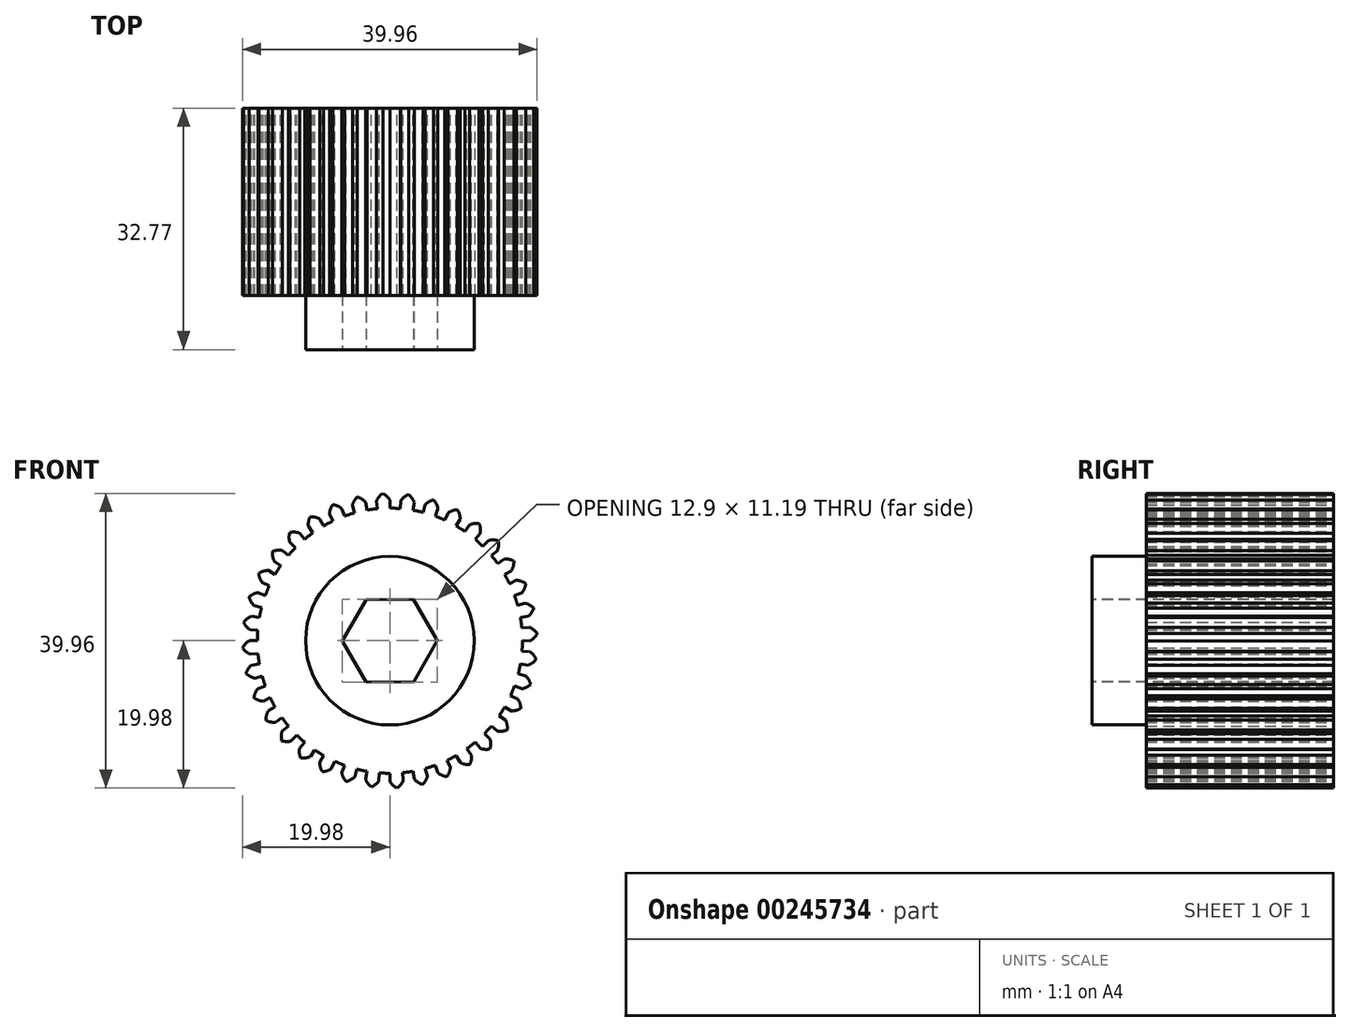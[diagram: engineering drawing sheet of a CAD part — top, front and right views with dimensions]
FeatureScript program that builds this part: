
annotation { "Feature Type Name" : "Feature", "Feature Type Description" : "" }
export const myFeature = defineFeature(function(context is Context, id is Id, definition is map)
    precondition{}
    {
        {
            var Q0;
            Q0=qCreatedBy(makeId("Front.planeOp"),FACE);
            var sketch = newSketch(context, id + "F0", { "sketchPlane" : qUnion([Q0])});
            skArc(sketch, "E0", {"start": v(0, 19.05) * mm, "mid": v(0, 19.05) * mm, "end": v(0, 19.05) * mm});
            skArc(sketch, "E1", {"start": v(-4.8, 17.33) * mm, "mid": v(-5.48, 17.13) * mm, "end": v(-6.15, 16.9) * mm});
            skLineSegment(sketch, "E2", {"start": v(-1.56, 17.83) * mm, "end": v(-1.57, 17.91) * mm});
            skLineSegment(sketch, "E3", {"start": v(0, 16.67) * mm, "end": v(0, 16.67) * mm});
            skLineSegment(sketch, "E4", {"start": v(-0.86, 17.88) * mm, "end": v(-0.86, 17.96) * mm});
            skArc(sketch, "E5.trimOffspring", {"start": v(0, 19.05) * mm, "mid": v(-0.4, 19.58) * mm, "end": v(-0.96, 19.98) * mm});
            skLineSegment(sketch, "E6.trimOffspring", {"start": v(0, 19.05) * mm, "end": v(0, 19.06) * mm});
            skArc(sketch, "E7.trimOffspring", {"start": v(-4.41, 17.44) * mm, "mid": v(-4.41, 17.44) * mm, "end": v(-4.41, 17.43) * mm});
            skPoint(sketch, "E8.trimOffspring.end.orphan", {"position": v(0, 30.11) * mm});
            skPoint(sketch, "E9.trimOffspring.end.orphan", {"position": v(-1.44, 30.11) * mm});
            skPoint(sketch, "E10.trimOffspring.end.orphan", {"position": v(-2.63, 30.11) * mm});
            skPoint(sketch, "E11.orphan", {"position": v(-14.18, 19.05) * mm});
            skPoint(sketch, "E12.trimOffspring.end.orphan", {"position": v(-14.18, 13.89) * mm});
            skLineSegment(sketch, "E13.trimOffspring", {"start": v(-1.66, 18.98) * mm, "end": v(-1.67, 19.05) * mm});
            skArc(sketch, "E14.trimOffspring", {"start": v(0.32, 17.9) * mm, "mid": v(0.32, 17.94) * mm, "end": v(0.32, 17.98) * mm});
            skLineSegment(sketch, "E15.trimOffspring", {"start": v(0, 17.9) * mm, "end": v(0, 17.98) * mm});
            skLineSegment(sketch, "E16", {"start": v(0, 19.05) * mm, "end": v(0, 17.98) * mm});
            skArc(sketch, "E17.MirrorCS", {"start": v(-1.83, 18.96) * mm, "mid": v(-1.46, 19.53) * mm, "end": v(-0.96, 19.98) * mm});
            skLineSegment(sketch, "E18.MirrorCS", {"start": v(-1.83, 18.96) * mm, "end": v(-1.72, 17.9) * mm});
            skArc(sketch, "E19.1.0", {"start": v(-3.3, 18.76) * mm, "mid": v(-3.8, 19.21) * mm, "end": v(-4.41, 19.5) * mm});
            skLineSegment(sketch, "E19.1.1", {"start": v(-3.3, 18.76) * mm, "end": v(-3.12, 17.7) * mm});
            skArc(sketch, "E19.1.2", {"start": v(-5.1, 18.36) * mm, "mid": v(-4.83, 18.98) * mm, "end": v(-4.41, 19.5) * mm});
            skLineSegment(sketch, "E19.1.3", {"start": v(-5.1, 18.36) * mm, "end": v(-4.8, 17.33) * mm});
            skArc(sketch, "E19.2.0", {"start": v(-6.51, 17.9) * mm, "mid": v(-7.08, 18.26) * mm, "end": v(-7.73, 18.44) * mm});
            skLineSegment(sketch, "E19.2.1", {"start": v(-6.51, 17.9) * mm, "end": v(-6.15, 16.9) * mm});
            skArc(sketch, "E19.2.2", {"start": v(-8.2, 17.2) * mm, "mid": v(-8.06, 17.85) * mm, "end": v(-7.73, 18.44) * mm});
            skLineSegment(sketch, "E19.2.3", {"start": v(-8.2, 17.2) * mm, "end": v(-7.74, 16.23) * mm});
            skArc(sketch, "E19.3.0", {"start": v(-9.52, 16.5) * mm, "mid": v(-10.15, 16.75) * mm, "end": v(-10.82, 16.82) * mm});
            skLineSegment(sketch, "E19.3.1", {"start": v(-9.52, 16.5) * mm, "end": v(-9, 15.57) * mm});
            skArc(sketch, "E19.3.2", {"start": v(-11.06, 15.5) * mm, "mid": v(-11.03, 16.18) * mm, "end": v(-10.82, 16.82) * mm});
            skLineSegment(sketch, "E19.3.3", {"start": v(-11.06, 15.5) * mm, "end": v(-10.44, 14.64) * mm});
            skArc(sketch, "E19.4.0", {"start": v(-12.24, 14.6) * mm, "mid": v(-12.9, 14.74) * mm, "end": v(-13.57, 14.69) * mm});
            skLineSegment(sketch, "E19.4.1", {"start": v(-12.24, 14.6) * mm, "end": v(-11.56, 13.78) * mm});
            skArc(sketch, "E19.4.2", {"start": v(-13.59, 13.35) * mm, "mid": v(-13.68, 14.02) * mm, "end": v(-13.57, 14.69) * mm});
            skLineSegment(sketch, "E19.4.3", {"start": v(-13.59, 13.35) * mm, "end": v(-12.82, 12.6) * mm});
            skArc(sketch, "E19.5.0", {"start": v(-14.59, 12.25) * mm, "mid": v(-15.26, 12.27) * mm, "end": v(-15.92, 12.1) * mm});
            skLineSegment(sketch, "E19.5.1", {"start": v(-14.59, 12.25) * mm, "end": v(-13.78, 11.56) * mm});
            skArc(sketch, "E19.5.2", {"start": v(-15.7, 10.8) * mm, "mid": v(-15.9, 11.43) * mm, "end": v(-15.92, 12.1) * mm});
            skLineSegment(sketch, "E19.5.3", {"start": v(-15.7, 10.8) * mm, "end": v(-14.82, 10.2) * mm});
            skArc(sketch, "E19.6.0", {"start": v(-16.5, 9.53) * mm, "mid": v(-17.16, 9.44) * mm, "end": v(-17.78, 9.16) * mm});
            skLineSegment(sketch, "E19.6.1", {"start": v(-16.5, 9.53) * mm, "end": v(-15.57, 9) * mm});
            skArc(sketch, "E19.6.2", {"start": v(-17.33, 7.9) * mm, "mid": v(-17.65, 8.5) * mm, "end": v(-17.78, 9.16) * mm});
            skLineSegment(sketch, "E19.6.3", {"start": v(-17.33, 7.9) * mm, "end": v(-16.36, 7.46) * mm});
            skArc(sketch, "E19.7.0", {"start": v(-17.9, 6.52) * mm, "mid": v(-18.54, 6.31) * mm, "end": v(-19.1, 5.93) * mm});
            skLineSegment(sketch, "E19.7.1", {"start": v(-17.9, 6.52) * mm, "end": v(-16.9, 6.15) * mm});
            skArc(sketch, "E19.7.2", {"start": v(-18.44, 4.77) * mm, "mid": v(-18.85, 5.3) * mm, "end": v(-19.1, 5.93) * mm});
            skLineSegment(sketch, "E19.7.3", {"start": v(-18.44, 4.77) * mm, "end": v(-17.4, 4.5) * mm});
            skArc(sketch, "E19.8.0", {"start": v(-18.76, 3.31) * mm, "mid": v(-19.36, 3) * mm, "end": v(-19.84, 2.53) * mm});
            skLineSegment(sketch, "E19.8.1", {"start": v(-18.76, 3.31) * mm, "end": v(-17.7, 3.12) * mm});
            skArc(sketch, "E19.8.2", {"start": v(-19, 1.5) * mm, "mid": v(-19.49, 1.95) * mm, "end": v(-19.84, 2.53) * mm});
            skLineSegment(sketch, "E19.8.3", {"start": v(-19, 1.5) * mm, "end": v(-17.93, 1.42) * mm});
            skArc(sketch, "E19.9.0", {"start": v(-19.05, 0) * mm, "mid": v(-19.58, -0.4) * mm, "end": v(-19.98, -0.96) * mm});
            skLineSegment(sketch, "E19.9.1", {"start": v(-19.05, 0) * mm, "end": v(-17.98, 0) * mm});
            skArc(sketch, "E19.9.2", {"start": v(-18.96, -1.83) * mm, "mid": v(-19.53, -1.46) * mm, "end": v(-19.98, -0.96) * mm});
            skLineSegment(sketch, "E19.9.3", {"start": v(-18.96, -1.83) * mm, "end": v(-17.9, -1.72) * mm});
            skArc(sketch, "E19.10.0", {"start": v(-18.76, -3.3) * mm, "mid": v(-19.21, -3.8) * mm, "end": v(-19.5, -4.41) * mm});
            skLineSegment(sketch, "E19.10.1", {"start": v(-18.76, -3.3) * mm, "end": v(-17.7, -3.12) * mm});
            skArc(sketch, "E19.10.2", {"start": v(-18.36, -5.1) * mm, "mid": v(-18.98, -4.83) * mm, "end": v(-19.5, -4.41) * mm});
            skLineSegment(sketch, "E19.10.3", {"start": v(-18.36, -5.1) * mm, "end": v(-17.33, -4.8) * mm});
            skArc(sketch, "E19.11.0", {"start": v(-17.9, -6.51) * mm, "mid": v(-18.26, -7.08) * mm, "end": v(-18.44, -7.73) * mm});
            skLineSegment(sketch, "E19.11.1", {"start": v(-17.9, -6.51) * mm, "end": v(-16.9, -6.15) * mm});
            skArc(sketch, "E19.11.2", {"start": v(-17.2, -8.2) * mm, "mid": v(-17.85, -8.06) * mm, "end": v(-18.44, -7.73) * mm});
            skLineSegment(sketch, "E19.11.3", {"start": v(-17.2, -8.2) * mm, "end": v(-16.23, -7.74) * mm});
            skArc(sketch, "E19.12.0", {"start": v(-16.5, -9.52) * mm, "mid": v(-16.75, -10.15) * mm, "end": v(-16.82, -10.82) * mm});
            skLineSegment(sketch, "E19.12.1", {"start": v(-16.5, -9.52) * mm, "end": v(-15.57, -9) * mm});
            skArc(sketch, "E19.12.2", {"start": v(-15.5, -11.06) * mm, "mid": v(-16.18, -11.03) * mm, "end": v(-16.82, -10.82) * mm});
            skLineSegment(sketch, "E19.12.3", {"start": v(-15.5, -11.06) * mm, "end": v(-14.64, -10.44) * mm});
            skArc(sketch, "E19.13.0", {"start": v(-14.6, -12.24) * mm, "mid": v(-14.74, -12.9) * mm, "end": v(-14.69, -13.57) * mm});
            skLineSegment(sketch, "E19.13.1", {"start": v(-14.6, -12.24) * mm, "end": v(-13.78, -11.56) * mm});
            skArc(sketch, "E19.13.2", {"start": v(-13.35, -13.59) * mm, "mid": v(-14.02, -13.68) * mm, "end": v(-14.69, -13.57) * mm});
            skLineSegment(sketch, "E19.13.3", {"start": v(-13.35, -13.59) * mm, "end": v(-12.6, -12.82) * mm});
            skArc(sketch, "E19.14.0", {"start": v(-12.25, -14.59) * mm, "mid": v(-12.27, -15.26) * mm, "end": v(-12.1, -15.92) * mm});
            skLineSegment(sketch, "E19.14.1", {"start": v(-12.25, -14.59) * mm, "end": v(-11.56, -13.78) * mm});
            skArc(sketch, "E19.14.2", {"start": v(-10.8, -15.7) * mm, "mid": v(-11.43, -15.9) * mm, "end": v(-12.1, -15.92) * mm});
            skLineSegment(sketch, "E19.14.3", {"start": v(-10.8, -15.7) * mm, "end": v(-10.2, -14.82) * mm});
            skArc(sketch, "E19.15.0", {"start": v(-9.53, -16.5) * mm, "mid": v(-9.44, -17.16) * mm, "end": v(-9.16, -17.78) * mm});
            skLineSegment(sketch, "E19.15.1", {"start": v(-9.53, -16.5) * mm, "end": v(-9, -15.57) * mm});
            skArc(sketch, "E19.15.2", {"start": v(-7.9, -17.33) * mm, "mid": v(-8.5, -17.65) * mm, "end": v(-9.16, -17.78) * mm});
            skLineSegment(sketch, "E19.15.3", {"start": v(-7.9, -17.33) * mm, "end": v(-7.46, -16.36) * mm});
            skArc(sketch, "E19.16.0", {"start": v(-6.52, -17.9) * mm, "mid": v(-6.31, -18.54) * mm, "end": v(-5.93, -19.1) * mm});
            skLineSegment(sketch, "E19.16.1", {"start": v(-6.52, -17.9) * mm, "end": v(-6.15, -16.9) * mm});
            skArc(sketch, "E19.16.2", {"start": v(-4.77, -18.44) * mm, "mid": v(-5.3, -18.85) * mm, "end": v(-5.93, -19.1) * mm});
            skLineSegment(sketch, "E19.16.3", {"start": v(-4.77, -18.44) * mm, "end": v(-4.5, -17.4) * mm});
            skArc(sketch, "E19.17.0", {"start": v(-3.31, -18.76) * mm, "mid": v(-3, -19.36) * mm, "end": v(-2.53, -19.84) * mm});
            skLineSegment(sketch, "E19.17.1", {"start": v(-3.31, -18.76) * mm, "end": v(-3.12, -17.7) * mm});
            skArc(sketch, "E19.17.2", {"start": v(-1.5, -19) * mm, "mid": v(-1.95, -19.49) * mm, "end": v(-2.53, -19.84) * mm});
            skLineSegment(sketch, "E19.17.3", {"start": v(-1.5, -19) * mm, "end": v(-1.42, -17.93) * mm});
            skArc(sketch, "E19.18.0", {"start": v(0, -19.05) * mm, "mid": v(0.4, -19.58) * mm, "end": v(0.96, -19.98) * mm});
            skLineSegment(sketch, "E19.18.1", {"start": v(0, -19.05) * mm, "end": v(0, -17.98) * mm});
            skArc(sketch, "E19.18.2", {"start": v(1.83, -18.96) * mm, "mid": v(1.46, -19.53) * mm, "end": v(0.96, -19.98) * mm});
            skLineSegment(sketch, "E19.18.3", {"start": v(1.83, -18.96) * mm, "end": v(1.72, -17.9) * mm});
            skArc(sketch, "E19.19.0", {"start": v(3.3, -18.76) * mm, "mid": v(3.8, -19.21) * mm, "end": v(4.41, -19.5) * mm});
            skLineSegment(sketch, "E19.19.1", {"start": v(3.3, -18.76) * mm, "end": v(3.12, -17.7) * mm});
            skArc(sketch, "E19.19.2", {"start": v(5.1, -18.36) * mm, "mid": v(4.83, -18.98) * mm, "end": v(4.41, -19.5) * mm});
            skLineSegment(sketch, "E19.19.3", {"start": v(5.1, -18.36) * mm, "end": v(4.8, -17.33) * mm});
            skArc(sketch, "E19.20.0", {"start": v(6.51, -17.9) * mm, "mid": v(7.08, -18.26) * mm, "end": v(7.73, -18.44) * mm});
            skLineSegment(sketch, "E19.20.1", {"start": v(6.51, -17.9) * mm, "end": v(6.15, -16.9) * mm});
            skArc(sketch, "E19.20.2", {"start": v(8.2, -17.2) * mm, "mid": v(8.06, -17.85) * mm, "end": v(7.73, -18.44) * mm});
            skLineSegment(sketch, "E19.20.3", {"start": v(8.2, -17.2) * mm, "end": v(7.74, -16.23) * mm});
            skArc(sketch, "E19.21.0", {"start": v(9.52, -16.5) * mm, "mid": v(10.15, -16.75) * mm, "end": v(10.82, -16.82) * mm});
            skLineSegment(sketch, "E19.21.1", {"start": v(9.52, -16.5) * mm, "end": v(9, -15.57) * mm});
            skArc(sketch, "E19.21.2", {"start": v(11.06, -15.5) * mm, "mid": v(11.03, -16.18) * mm, "end": v(10.82, -16.82) * mm});
            skLineSegment(sketch, "E19.21.3", {"start": v(11.06, -15.5) * mm, "end": v(10.44, -14.64) * mm});
            skArc(sketch, "E19.22.0", {"start": v(12.24, -14.6) * mm, "mid": v(12.9, -14.74) * mm, "end": v(13.57, -14.69) * mm});
            skLineSegment(sketch, "E19.22.1", {"start": v(12.24, -14.6) * mm, "end": v(11.56, -13.78) * mm});
            skArc(sketch, "E19.22.2", {"start": v(13.59, -13.35) * mm, "mid": v(13.68, -14.02) * mm, "end": v(13.57, -14.69) * mm});
            skLineSegment(sketch, "E19.22.3", {"start": v(13.59, -13.35) * mm, "end": v(12.82, -12.6) * mm});
            skArc(sketch, "E19.23.0", {"start": v(14.59, -12.25) * mm, "mid": v(15.26, -12.27) * mm, "end": v(15.92, -12.1) * mm});
            skLineSegment(sketch, "E19.23.1", {"start": v(14.59, -12.25) * mm, "end": v(13.78, -11.56) * mm});
            skArc(sketch, "E19.23.2", {"start": v(15.7, -10.8) * mm, "mid": v(15.9, -11.43) * mm, "end": v(15.92, -12.1) * mm});
            skLineSegment(sketch, "E19.23.3", {"start": v(15.7, -10.8) * mm, "end": v(14.82, -10.2) * mm});
            skArc(sketch, "E19.24.0", {"start": v(16.5, -9.53) * mm, "mid": v(17.16, -9.44) * mm, "end": v(17.78, -9.16) * mm});
            skLineSegment(sketch, "E19.24.1", {"start": v(16.5, -9.53) * mm, "end": v(15.57, -9) * mm});
            skArc(sketch, "E19.24.2", {"start": v(17.33, -7.9) * mm, "mid": v(17.65, -8.5) * mm, "end": v(17.78, -9.16) * mm});
            skLineSegment(sketch, "E19.24.3", {"start": v(17.33, -7.9) * mm, "end": v(16.36, -7.46) * mm});
            skArc(sketch, "E19.25.0", {"start": v(17.9, -6.52) * mm, "mid": v(18.54, -6.31) * mm, "end": v(19.1, -5.93) * mm});
            skLineSegment(sketch, "E19.25.1", {"start": v(17.9, -6.52) * mm, "end": v(16.9, -6.15) * mm});
            skArc(sketch, "E19.25.2", {"start": v(18.44, -4.77) * mm, "mid": v(18.85, -5.3) * mm, "end": v(19.1, -5.93) * mm});
            skLineSegment(sketch, "E19.25.3", {"start": v(18.44, -4.77) * mm, "end": v(17.4, -4.5) * mm});
            skArc(sketch, "E19.26.0", {"start": v(18.76, -3.31) * mm, "mid": v(19.36, -3) * mm, "end": v(19.84, -2.53) * mm});
            skLineSegment(sketch, "E19.26.1", {"start": v(18.76, -3.31) * mm, "end": v(17.7, -3.12) * mm});
            skArc(sketch, "E19.26.2", {"start": v(19, -1.5) * mm, "mid": v(19.49, -1.95) * mm, "end": v(19.84, -2.53) * mm});
            skLineSegment(sketch, "E19.26.3", {"start": v(19, -1.5) * mm, "end": v(17.93, -1.42) * mm});
            skArc(sketch, "E19.27.0", {"start": v(19.05, 0) * mm, "mid": v(19.58, 0.4) * mm, "end": v(19.98, 0.96) * mm});
            skLineSegment(sketch, "E19.27.1", {"start": v(19.05, 0) * mm, "end": v(17.98, 0) * mm});
            skArc(sketch, "E19.27.2", {"start": v(18.96, 1.83) * mm, "mid": v(19.53, 1.46) * mm, "end": v(19.98, 0.96) * mm});
            skLineSegment(sketch, "E19.27.3", {"start": v(18.96, 1.83) * mm, "end": v(17.9, 1.72) * mm});
            skArc(sketch, "E19.28.0", {"start": v(18.76, 3.3) * mm, "mid": v(19.21, 3.8) * mm, "end": v(19.5, 4.41) * mm});
            skLineSegment(sketch, "E19.28.1", {"start": v(18.76, 3.3) * mm, "end": v(17.7, 3.12) * mm});
            skArc(sketch, "E19.28.2", {"start": v(18.36, 5.1) * mm, "mid": v(18.98, 4.83) * mm, "end": v(19.5, 4.41) * mm});
            skLineSegment(sketch, "E19.28.3", {"start": v(18.36, 5.1) * mm, "end": v(17.33, 4.8) * mm});
            skArc(sketch, "E19.29.0", {"start": v(17.9, 6.51) * mm, "mid": v(18.26, 7.08) * mm, "end": v(18.44, 7.73) * mm});
            skLineSegment(sketch, "E19.29.1", {"start": v(17.9, 6.51) * mm, "end": v(16.9, 6.15) * mm});
            skArc(sketch, "E19.29.2", {"start": v(17.2, 8.2) * mm, "mid": v(17.85, 8.06) * mm, "end": v(18.44, 7.73) * mm});
            skLineSegment(sketch, "E19.29.3", {"start": v(17.2, 8.2) * mm, "end": v(16.23, 7.74) * mm});
            skArc(sketch, "E19.30.0", {"start": v(16.5, 9.52) * mm, "mid": v(16.75, 10.15) * mm, "end": v(16.82, 10.82) * mm});
            skLineSegment(sketch, "E19.30.1", {"start": v(16.5, 9.52) * mm, "end": v(15.57, 9) * mm});
            skArc(sketch, "E19.30.2", {"start": v(15.5, 11.06) * mm, "mid": v(16.18, 11.03) * mm, "end": v(16.82, 10.82) * mm});
            skLineSegment(sketch, "E19.30.3", {"start": v(15.5, 11.06) * mm, "end": v(14.64, 10.44) * mm});
            skArc(sketch, "E19.31.0", {"start": v(14.6, 12.24) * mm, "mid": v(14.74, 12.9) * mm, "end": v(14.69, 13.57) * mm});
            skLineSegment(sketch, "E19.31.1", {"start": v(14.6, 12.24) * mm, "end": v(13.78, 11.56) * mm});
            skArc(sketch, "E19.31.2", {"start": v(13.35, 13.59) * mm, "mid": v(14.02, 13.68) * mm, "end": v(14.69, 13.57) * mm});
            skLineSegment(sketch, "E19.31.3", {"start": v(13.35, 13.59) * mm, "end": v(12.6, 12.82) * mm});
            skArc(sketch, "E19.32.0", {"start": v(12.25, 14.59) * mm, "mid": v(12.27, 15.26) * mm, "end": v(12.1, 15.92) * mm});
            skLineSegment(sketch, "E19.32.1", {"start": v(12.25, 14.59) * mm, "end": v(11.56, 13.78) * mm});
            skArc(sketch, "E19.32.2", {"start": v(10.8, 15.7) * mm, "mid": v(11.43, 15.9) * mm, "end": v(12.1, 15.92) * mm});
            skLineSegment(sketch, "E19.32.3", {"start": v(10.8, 15.7) * mm, "end": v(10.2, 14.82) * mm});
            skArc(sketch, "E19.33.0", {"start": v(9.53, 16.5) * mm, "mid": v(9.44, 17.16) * mm, "end": v(9.16, 17.78) * mm});
            skLineSegment(sketch, "E19.33.1", {"start": v(9.53, 16.5) * mm, "end": v(9, 15.57) * mm});
            skArc(sketch, "E19.33.2", {"start": v(7.9, 17.33) * mm, "mid": v(8.5, 17.65) * mm, "end": v(9.16, 17.78) * mm});
            skLineSegment(sketch, "E19.33.3", {"start": v(7.9, 17.33) * mm, "end": v(7.46, 16.36) * mm});
            skArc(sketch, "E19.34.0", {"start": v(6.52, 17.9) * mm, "mid": v(6.31, 18.54) * mm, "end": v(5.93, 19.1) * mm});
            skLineSegment(sketch, "E19.34.1", {"start": v(6.52, 17.9) * mm, "end": v(6.15, 16.9) * mm});
            skArc(sketch, "E19.34.2", {"start": v(4.77, 18.44) * mm, "mid": v(5.3, 18.85) * mm, "end": v(5.93, 19.1) * mm});
            skLineSegment(sketch, "E19.34.3", {"start": v(4.77, 18.44) * mm, "end": v(4.5, 17.4) * mm});
            skArc(sketch, "E19.35.0", {"start": v(3.31, 18.76) * mm, "mid": v(3, 19.36) * mm, "end": v(2.53, 19.84) * mm});
            skLineSegment(sketch, "E19.35.1", {"start": v(3.31, 18.76) * mm, "end": v(3.12, 17.7) * mm});
            skArc(sketch, "E19.35.2", {"start": v(1.5, 19) * mm, "mid": v(1.95, 19.49) * mm, "end": v(2.53, 19.84) * mm});
            skLineSegment(sketch, "E19.35.3", {"start": v(1.5, 19) * mm, "end": v(1.42, 17.93) * mm});
            skArc(sketch, "E20.trimOffspring", {"start": v(-7.74, 16.23) * mm, "mid": v(-8.37, 15.92) * mm, "end": v(-9, 15.57) * mm});
            skArc(sketch, "E21.trimOffspring", {"start": v(-10.44, 14.64) * mm, "mid": v(-11, 14.22) * mm, "end": v(-11.56, 13.78) * mm});
            skArc(sketch, "E22.trimOffspring", {"start": v(-12.82, 12.6) * mm, "mid": v(-13.3, 12.1) * mm, "end": v(-13.78, 11.56) * mm});
            skArc(sketch, "E23.trimOffspring", {"start": v(-14.82, 10.2) * mm, "mid": v(-15.2, 9.6) * mm, "end": v(-15.57, 9) * mm});
            skArc(sketch, "E24.trimOffspring", {"start": v(-16.36, 7.46) * mm, "mid": v(-16.64, 6.81) * mm, "end": v(-16.9, 6.15) * mm});
            skArc(sketch, "E25.trimOffspring", {"start": v(-17.4, 4.5) * mm, "mid": v(-17.57, 3.82) * mm, "end": v(-17.7, 3.12) * mm});
            skArc(sketch, "E26.trimOffspring", {"start": v(-17.93, 1.42) * mm, "mid": v(-17.97, 0.7) * mm, "end": v(-17.98, 0) * mm});
            skArc(sketch, "E27.trimOffspring", {"start": v(-17.9, -1.72) * mm, "mid": v(-17.82, -2.42) * mm, "end": v(-17.7, -3.12) * mm});
            skArc(sketch, "E28.trimOffspring", {"start": v(-17.33, -4.8) * mm, "mid": v(-17.13, -5.48) * mm, "end": v(-16.9, -6.15) * mm});
            skArc(sketch, "E29.trimOffspring", {"start": v(-16.23, -7.74) * mm, "mid": v(-15.92, -8.37) * mm, "end": v(-15.57, -9) * mm});
            skArc(sketch, "E30.trimOffspring", {"start": v(-14.64, -10.44) * mm, "mid": v(-14.22, -11) * mm, "end": v(-13.78, -11.56) * mm});
            skArc(sketch, "E31.trimOffspring", {"start": v(-12.6, -12.82) * mm, "mid": v(-12.1, -13.3) * mm, "end": v(-11.56, -13.78) * mm});
            skArc(sketch, "E32.trimOffspring", {"start": v(-10.2, -14.82) * mm, "mid": v(-9.6, -15.2) * mm, "end": v(-9, -15.57) * mm});
            skArc(sketch, "E33.trimOffspring", {"start": v(-7.46, -16.36) * mm, "mid": v(-6.81, -16.64) * mm, "end": v(-6.15, -16.9) * mm});
            skArc(sketch, "E34.trimOffspring", {"start": v(-4.5, -17.4) * mm, "mid": v(-3.82, -17.57) * mm, "end": v(-3.12, -17.7) * mm});
            skArc(sketch, "E35.trimOffspring", {"start": v(-1.42, -17.93) * mm, "mid": v(-0.7, -17.97) * mm, "end": v(0, -17.98) * mm});
            skArc(sketch, "E36.trimOffspring", {"start": v(1.72, -17.9) * mm, "mid": v(2.42, -17.82) * mm, "end": v(3.12, -17.7) * mm});
            skArc(sketch, "E37.trimOffspring", {"start": v(4.8, -17.33) * mm, "mid": v(5.48, -17.13) * mm, "end": v(6.15, -16.9) * mm});
            skArc(sketch, "E38.trimOffspring", {"start": v(7.74, -16.23) * mm, "mid": v(8.37, -15.92) * mm, "end": v(9, -15.57) * mm});
            skArc(sketch, "E39.trimOffspring", {"start": v(10.44, -14.64) * mm, "mid": v(11, -14.22) * mm, "end": v(11.56, -13.78) * mm});
            skArc(sketch, "E40.trimOffspring", {"start": v(12.82, -12.6) * mm, "mid": v(13.3, -12.1) * mm, "end": v(13.78, -11.56) * mm});
            skArc(sketch, "E41.trimOffspring", {"start": v(14.82, -10.2) * mm, "mid": v(15.2, -9.6) * mm, "end": v(15.57, -9) * mm});
            skArc(sketch, "E42.trimOffspring", {"start": v(16.36, -7.46) * mm, "mid": v(16.64, -6.81) * mm, "end": v(16.9, -6.15) * mm});
            skArc(sketch, "E43.trimOffspring", {"start": v(17.4, -4.5) * mm, "mid": v(17.57, -3.82) * mm, "end": v(17.7, -3.12) * mm});
            skArc(sketch, "E44.trimOffspring", {"start": v(17.93, -1.42) * mm, "mid": v(17.97, -0.7) * mm, "end": v(17.98, 0) * mm});
            skArc(sketch, "E45.trimOffspring", {"start": v(17.9, 1.72) * mm, "mid": v(17.82, 2.42) * mm, "end": v(17.7, 3.12) * mm});
            skArc(sketch, "E46.trimOffspring", {"start": v(17.33, 4.8) * mm, "mid": v(17.13, 5.48) * mm, "end": v(16.9, 6.15) * mm});
            skArc(sketch, "E47.trimOffspring", {"start": v(16.23, 7.74) * mm, "mid": v(15.92, 8.37) * mm, "end": v(15.57, 9) * mm});
            skArc(sketch, "E48.trimOffspring", {"start": v(14.64, 10.44) * mm, "mid": v(14.22, 11) * mm, "end": v(13.78, 11.56) * mm});
            skArc(sketch, "E49.trimOffspring", {"start": v(12.6, 12.82) * mm, "mid": v(12.1, 13.3) * mm, "end": v(11.56, 13.78) * mm});
            skArc(sketch, "E50.trimOffspring", {"start": v(10.2, 14.82) * mm, "mid": v(9.6, 15.2) * mm, "end": v(9, 15.57) * mm});
            skArc(sketch, "E51.trimOffspring", {"start": v(7.46, 16.36) * mm, "mid": v(6.81, 16.64) * mm, "end": v(6.15, 16.9) * mm});
            skArc(sketch, "E52.trimOffspring", {"start": v(4.5, 17.4) * mm, "mid": v(3.82, 17.57) * mm, "end": v(3.12, 17.7) * mm});
            skArc(sketch, "E53.trimOffspring", {"start": v(1.42, 17.93) * mm, "mid": v(0.7, 17.97) * mm, "end": v(0, 17.98) * mm});
            skArc(sketch, "E54.trimOffspring", {"start": v(-1.57, 17.91) * mm, "mid": v(-2.35, 17.83) * mm, "end": v(-3.12, 17.7) * mm});
            skSolve(sketch);
        }
        {
            var Q0;
            Q0 = qSketchRegion(id + "F0", true);
            extrude(context, id + "F1", {"entities" : qUnion([Q0]), "depth" : 25.4 * mm});
        }
        {
            var Q0;
            Q0=makeQuery(id+"F1.opExtrude","CAP_FACE",FACE,{"disambiguationData":[OSD([sQuery(id+"F0.wireOp",EDGE,"E1"),sQuery(id+"F0.wireOp",EDGE,"E5.trimOffspring"),sQuery(id+"F0.wireOp",EDGE,"E16"),sQuery(id+"F0.wireOp",EDGE,"E17.MirrorCS"),sQuery(id+"F0.wireOp",EDGE,"E18.MirrorCS"),sQuery(id+"F0.wireOp",EDGE,"E19.1.0"),sQuery(id+"F0.wireOp",EDGE,"E19.1.1"),sQuery(id+"F0.wireOp",EDGE,"E19.1.2"),sQuery(id+"F0.wireOp",EDGE,"E19.1.3"),sQuery(id+"F0.wireOp",EDGE,"E19.2.0"),sQuery(id+"F0.wireOp",EDGE,"E19.2.1"),sQuery(id+"F0.wireOp",EDGE,"E19.2.2"),sQuery(id+"F0.wireOp",EDGE,"E19.2.3"),sQuery(id+"F0.wireOp",EDGE,"E19.3.0"),sQuery(id+"F0.wireOp",EDGE,"E19.3.1"),sQuery(id+"F0.wireOp",EDGE,"E19.3.2"),sQuery(id+"F0.wireOp",EDGE,"E19.3.3"),sQuery(id+"F0.wireOp",EDGE,"E19.4.0"),sQuery(id+"F0.wireOp",EDGE,"E19.4.1"),sQuery(id+"F0.wireOp",EDGE,"E19.4.2"),sQuery(id+"F0.wireOp",EDGE,"E19.4.3"),sQuery(id+"F0.wireOp",EDGE,"E19.5.0"),sQuery(id+"F0.wireOp",EDGE,"E19.5.1"),sQuery(id+"F0.wireOp",EDGE,"E19.5.2"),sQuery(id+"F0.wireOp",EDGE,"E19.5.3"),sQuery(id+"F0.wireOp",EDGE,"E19.6.0"),sQuery(id+"F0.wireOp",EDGE,"E19.6.1"),sQuery(id+"F0.wireOp",EDGE,"E19.6.2"),sQuery(id+"F0.wireOp",EDGE,"E19.6.3"),sQuery(id+"F0.wireOp",EDGE,"E19.7.0"),sQuery(id+"F0.wireOp",EDGE,"E19.7.1"),sQuery(id+"F0.wireOp",EDGE,"E19.7.2"),sQuery(id+"F0.wireOp",EDGE,"E19.7.3"),sQuery(id+"F0.wireOp",EDGE,"E19.8.0"),sQuery(id+"F0.wireOp",EDGE,"E19.8.1"),sQuery(id+"F0.wireOp",EDGE,"E19.8.2"),sQuery(id+"F0.wireOp",EDGE,"E19.8.3"),sQuery(id+"F0.wireOp",EDGE,"E19.9.0"),sQuery(id+"F0.wireOp",EDGE,"E19.9.1"),sQuery(id+"F0.wireOp",EDGE,"E19.9.2"),sQuery(id+"F0.wireOp",EDGE,"E19.9.3"),sQuery(id+"F0.wireOp",EDGE,"E19.10.0"),sQuery(id+"F0.wireOp",EDGE,"E19.10.1"),sQuery(id+"F0.wireOp",EDGE,"E19.10.2"),sQuery(id+"F0.wireOp",EDGE,"E19.10.3"),sQuery(id+"F0.wireOp",EDGE,"E19.11.0"),sQuery(id+"F0.wireOp",EDGE,"E19.11.1"),sQuery(id+"F0.wireOp",EDGE,"E19.11.2"),sQuery(id+"F0.wireOp",EDGE,"E19.11.3"),sQuery(id+"F0.wireOp",EDGE,"E19.12.0"),sQuery(id+"F0.wireOp",EDGE,"E19.12.1"),sQuery(id+"F0.wireOp",EDGE,"E19.12.2"),sQuery(id+"F0.wireOp",EDGE,"E19.12.3"),sQuery(id+"F0.wireOp",EDGE,"E19.13.0"),sQuery(id+"F0.wireOp",EDGE,"E19.13.1"),sQuery(id+"F0.wireOp",EDGE,"E19.13.2"),sQuery(id+"F0.wireOp",EDGE,"E19.13.3"),sQuery(id+"F0.wireOp",EDGE,"E19.14.0"),sQuery(id+"F0.wireOp",EDGE,"E19.14.1"),sQuery(id+"F0.wireOp",EDGE,"E19.14.2"),sQuery(id+"F0.wireOp",EDGE,"E19.14.3"),sQuery(id+"F0.wireOp",EDGE,"E19.15.0"),sQuery(id+"F0.wireOp",EDGE,"E19.15.1"),sQuery(id+"F0.wireOp",EDGE,"E19.15.2"),sQuery(id+"F0.wireOp",EDGE,"E19.15.3"),sQuery(id+"F0.wireOp",EDGE,"E19.16.0"),sQuery(id+"F0.wireOp",EDGE,"E19.16.1"),sQuery(id+"F0.wireOp",EDGE,"E19.16.2"),sQuery(id+"F0.wireOp",EDGE,"E19.16.3"),sQuery(id+"F0.wireOp",EDGE,"E19.17.0"),sQuery(id+"F0.wireOp",EDGE,"E19.17.1"),sQuery(id+"F0.wireOp",EDGE,"E19.17.2"),sQuery(id+"F0.wireOp",EDGE,"E19.17.3"),sQuery(id+"F0.wireOp",EDGE,"E19.18.0"),sQuery(id+"F0.wireOp",EDGE,"E19.18.1"),sQuery(id+"F0.wireOp",EDGE,"E19.18.2"),sQuery(id+"F0.wireOp",EDGE,"E19.18.3"),sQuery(id+"F0.wireOp",EDGE,"E19.19.0"),sQuery(id+"F0.wireOp",EDGE,"E19.19.1"),sQuery(id+"F0.wireOp",EDGE,"E19.19.2"),sQuery(id+"F0.wireOp",EDGE,"E19.19.3"),sQuery(id+"F0.wireOp",EDGE,"E19.20.0"),sQuery(id+"F0.wireOp",EDGE,"E19.20.1"),sQuery(id+"F0.wireOp",EDGE,"E19.20.2"),sQuery(id+"F0.wireOp",EDGE,"E19.20.3"),sQuery(id+"F0.wireOp",EDGE,"E19.21.0"),sQuery(id+"F0.wireOp",EDGE,"E19.21.1"),sQuery(id+"F0.wireOp",EDGE,"E19.21.2"),sQuery(id+"F0.wireOp",EDGE,"E19.21.3"),sQuery(id+"F0.wireOp",EDGE,"E19.22.0"),sQuery(id+"F0.wireOp",EDGE,"E19.22.1"),sQuery(id+"F0.wireOp",EDGE,"E19.22.2"),sQuery(id+"F0.wireOp",EDGE,"E19.22.3"),sQuery(id+"F0.wireOp",EDGE,"E19.23.0"),sQuery(id+"F0.wireOp",EDGE,"E19.23.1"),sQuery(id+"F0.wireOp",EDGE,"E19.23.2"),sQuery(id+"F0.wireOp",EDGE,"E19.23.3"),sQuery(id+"F0.wireOp",EDGE,"E19.24.0"),sQuery(id+"F0.wireOp",EDGE,"E19.24.1"),sQuery(id+"F0.wireOp",EDGE,"E19.24.2"),sQuery(id+"F0.wireOp",EDGE,"E19.24.3"),sQuery(id+"F0.wireOp",EDGE,"E19.25.0"),sQuery(id+"F0.wireOp",EDGE,"E19.25.1"),sQuery(id+"F0.wireOp",EDGE,"E19.25.2"),sQuery(id+"F0.wireOp",EDGE,"E19.25.3"),sQuery(id+"F0.wireOp",EDGE,"E19.26.0"),sQuery(id+"F0.wireOp",EDGE,"E19.26.1"),sQuery(id+"F0.wireOp",EDGE,"E19.26.2"),sQuery(id+"F0.wireOp",EDGE,"E19.26.3"),sQuery(id+"F0.wireOp",EDGE,"E19.27.0"),sQuery(id+"F0.wireOp",EDGE,"E19.27.1"),sQuery(id+"F0.wireOp",EDGE,"E19.27.2"),sQuery(id+"F0.wireOp",EDGE,"E19.27.3"),sQuery(id+"F0.wireOp",EDGE,"E19.28.0"),sQuery(id+"F0.wireOp",EDGE,"E19.28.1"),sQuery(id+"F0.wireOp",EDGE,"E19.28.2"),sQuery(id+"F0.wireOp",EDGE,"E19.28.3"),sQuery(id+"F0.wireOp",EDGE,"E19.29.0"),sQuery(id+"F0.wireOp",EDGE,"E19.29.1"),sQuery(id+"F0.wireOp",EDGE,"E19.29.2"),sQuery(id+"F0.wireOp",EDGE,"E19.29.3"),sQuery(id+"F0.wireOp",EDGE,"E19.30.0"),sQuery(id+"F0.wireOp",EDGE,"E19.30.1"),sQuery(id+"F0.wireOp",EDGE,"E19.30.2"),sQuery(id+"F0.wireOp",EDGE,"E19.30.3"),sQuery(id+"F0.wireOp",EDGE,"E19.31.0"),sQuery(id+"F0.wireOp",EDGE,"E19.31.1"),sQuery(id+"F0.wireOp",EDGE,"E19.31.2"),sQuery(id+"F0.wireOp",EDGE,"E19.31.3"),sQuery(id+"F0.wireOp",EDGE,"E19.32.0"),sQuery(id+"F0.wireOp",EDGE,"E19.32.1"),sQuery(id+"F0.wireOp",EDGE,"E19.32.2"),sQuery(id+"F0.wireOp",EDGE,"E19.32.3"),sQuery(id+"F0.wireOp",EDGE,"E19.33.0"),sQuery(id+"F0.wireOp",EDGE,"E19.33.1"),sQuery(id+"F0.wireOp",EDGE,"E19.33.2"),sQuery(id+"F0.wireOp",EDGE,"E19.33.3"),sQuery(id+"F0.wireOp",EDGE,"E19.34.0"),sQuery(id+"F0.wireOp",EDGE,"E19.34.1"),sQuery(id+"F0.wireOp",EDGE,"E19.34.2"),sQuery(id+"F0.wireOp",EDGE,"E19.34.3"),sQuery(id+"F0.wireOp",EDGE,"E19.35.0"),sQuery(id+"F0.wireOp",EDGE,"E19.35.1"),sQuery(id+"F0.wireOp",EDGE,"E19.35.2"),sQuery(id+"F0.wireOp",EDGE,"E19.35.3"),sQuery(id+"F0.wireOp",EDGE,"E20.trimOffspring"),sQuery(id+"F0.wireOp",EDGE,"E21.trimOffspring"),sQuery(id+"F0.wireOp",EDGE,"E22.trimOffspring"),sQuery(id+"F0.wireOp",EDGE,"E23.trimOffspring"),sQuery(id+"F0.wireOp",EDGE,"E24.trimOffspring"),sQuery(id+"F0.wireOp",EDGE,"E25.trimOffspring"),sQuery(id+"F0.wireOp",EDGE,"E26.trimOffspring"),sQuery(id+"F0.wireOp",EDGE,"E27.trimOffspring"),sQuery(id+"F0.wireOp",EDGE,"E28.trimOffspring"),sQuery(id+"F0.wireOp",EDGE,"E29.trimOffspring"),sQuery(id+"F0.wireOp",EDGE,"E30.trimOffspring"),sQuery(id+"F0.wireOp",EDGE,"E31.trimOffspring"),sQuery(id+"F0.wireOp",EDGE,"E32.trimOffspring"),sQuery(id+"F0.wireOp",EDGE,"E33.trimOffspring"),sQuery(id+"F0.wireOp",EDGE,"E34.trimOffspring"),sQuery(id+"F0.wireOp",EDGE,"E35.trimOffspring"),sQuery(id+"F0.wireOp",EDGE,"E36.trimOffspring"),sQuery(id+"F0.wireOp",EDGE,"E37.trimOffspring"),sQuery(id+"F0.wireOp",EDGE,"E38.trimOffspring"),sQuery(id+"F0.wireOp",EDGE,"E39.trimOffspring"),sQuery(id+"F0.wireOp",EDGE,"E40.trimOffspring"),sQuery(id+"F0.wireOp",EDGE,"E41.trimOffspring"),sQuery(id+"F0.wireOp",EDGE,"E42.trimOffspring"),sQuery(id+"F0.wireOp",EDGE,"E43.trimOffspring"),sQuery(id+"F0.wireOp",EDGE,"E44.trimOffspring"),sQuery(id+"F0.wireOp",EDGE,"E45.trimOffspring"),sQuery(id+"F0.wireOp",EDGE,"E46.trimOffspring"),sQuery(id+"F0.wireOp",EDGE,"E47.trimOffspring"),sQuery(id+"F0.wireOp",EDGE,"E48.trimOffspring"),sQuery(id+"F0.wireOp",EDGE,"E49.trimOffspring"),sQuery(id+"F0.wireOp",EDGE,"E50.trimOffspring"),sQuery(id+"F0.wireOp",EDGE,"E51.trimOffspring"),sQuery(id+"F0.wireOp",EDGE,"E52.trimOffspring"),sQuery(id+"F0.wireOp",EDGE,"E53.trimOffspring"),sQuery(id+"F0.wireOp",EDGE,"E54.trimOffspring")])],"isStart":false});
            var sketch = newSketch(context, id + "F2", { "sketchPlane" : qUnion([Q0])});
            skCircle(sketch, "E55", {"center": v(0, 0) * mm, "radius": 11.43 * mm});
            skSolve(sketch);
        }
        {
            var Q0;
            Q0 = qSketchRegion(id + "F2", true);
            extrude(context, id + "F3", {"entities" : qUnion([Q0]), "operationType" : NewBodyOperationType.ADD, "depth" : 7.37 * mm});
        }
        {
            var Q0;
            Q0=makeQuery(id+"F3.opExtrude","CAP_FACE",FACE,{"disambiguationData":[OSD([sQuery(id+"F2.wireOp",EDGE,"E55")])],"isStart":false});
            var sketch = newSketch(context, id + "F4", { "sketchPlane" : qUnion([Q0])});
            skCircle(sketch, "E56.cCircle", {"center": v(0, 0) * mm, "radius": 6.45 * mm, "construction": true});
            skLineSegment(sketch, "E56.0", {"start": v(-3.24, 5.58) * mm, "end": v(3.22, 5.6) * mm});
            skLineSegment(sketch, "E56.1", {"start": v(3.22, 5.6) * mm, "end": v(6.45, 0.01) * mm});
            skLineSegment(sketch, "E56.2", {"start": v(6.45, 0.01) * mm, "end": v(3.24, -5.58) * mm});
            skLineSegment(sketch, "E56.3", {"start": v(3.24, -5.58) * mm, "end": v(-3.22, -5.6) * mm});
            skLineSegment(sketch, "E56.4", {"start": v(-3.22, -5.6) * mm, "end": v(-6.45, -0.01) * mm});
            skLineSegment(sketch, "E56.5", {"start": v(-6.45, -0.01) * mm, "end": v(-3.24, 5.58) * mm});
            skSolve(sketch);
        }
        {
            var Q0;
            Q0 = qSketchRegion(id + "F4", true);
            extrude(context, id + "F5", {"entities" : qUnion([Q0]), "operationType" : NewBodyOperationType.REMOVE, "oppositeDirection" : true, "depth" : 254 * mm});
        }
    });
